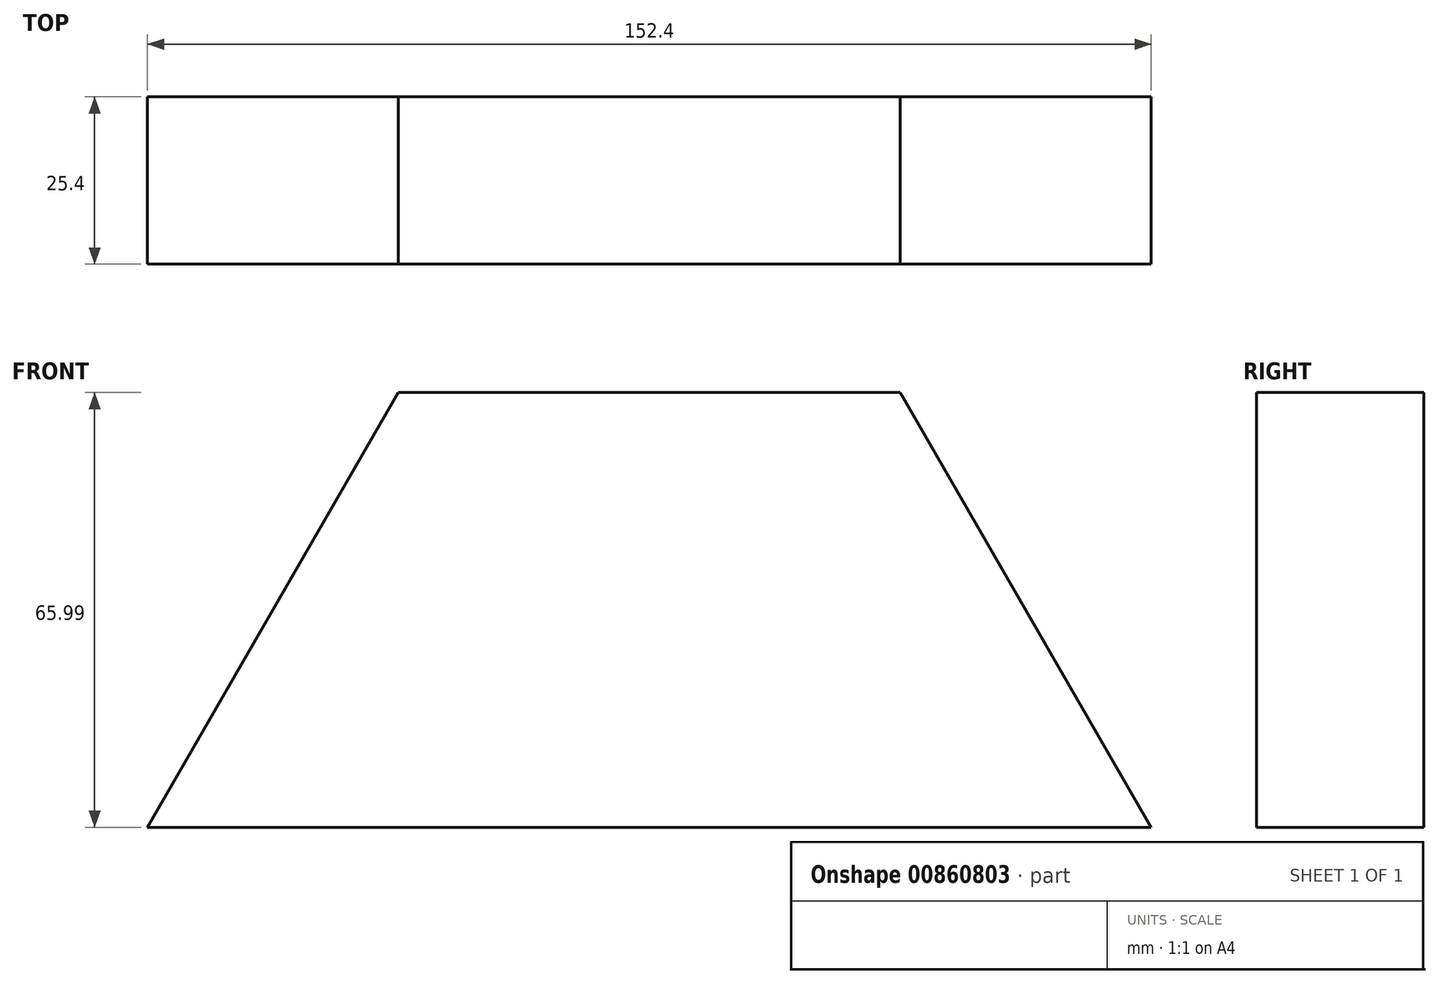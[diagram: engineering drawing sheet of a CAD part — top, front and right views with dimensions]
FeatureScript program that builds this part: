
annotation { "Feature Type Name" : "Feature", "Feature Type Description" : "" }
export const myFeature = defineFeature(function(context is Context, id is Id, definition is map)
    precondition{}
    {
        {
            var Q0;
            Q0=qCreatedBy(makeId("Front.planeOp"),FACE);
            var sketch = newSketch(context, id + "F0", { "sketchPlane" : qUnion([Q0])});
            skLineSegment(sketch, "E0", {"start": v(-49.84, -32.76) * mm, "end": v(102.56, -32.76) * mm});
            skLineSegment(sketch, "E1", {"start": v(102.56, -32.76) * mm, "end": v(64.46, 33.23) * mm});
            skLineSegment(sketch, "E2", {"start": v(64.46, 33.23) * mm, "end": v(-11.74, 33.23) * mm});
            skLineSegment(sketch, "E3", {"start": v(-11.74, 33.23) * mm, "end": v(-49.84, -32.76) * mm});
            skSolve(sketch);
        }
        {
            var Q0;
            Q0 = qSketchRegion(id + "F0", true);
            extrude(context, id + "F1", {"entities" : qUnion([Q0]), "depth" : 25.4 * mm, "offsetDistance" : 25.4 * mm});
        }
    });
